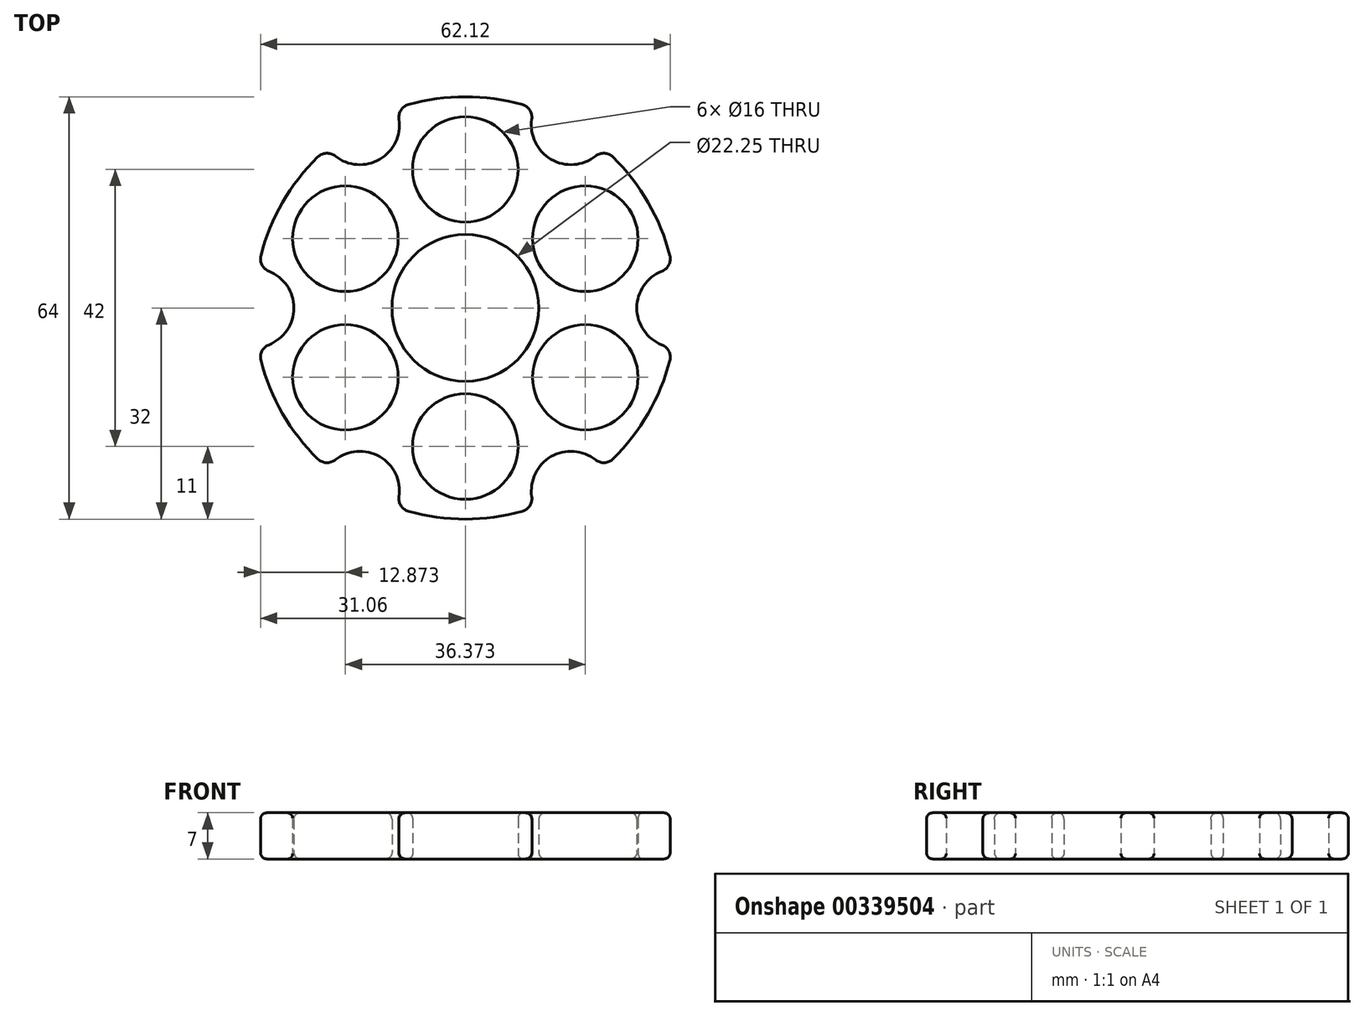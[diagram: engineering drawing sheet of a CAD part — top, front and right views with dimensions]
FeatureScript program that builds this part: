
annotation { "Feature Type Name" : "Feature", "Feature Type Description" : "" }
export const myFeature = defineFeature(function(context is Context, id is Id, definition is map)
    precondition{}
    {
        {
            var Q0;
            Q0=qCreatedBy(makeId("Top.planeOp"),FACE);
            var sketch = newSketch(context, id + "F0", { "sketchPlane" : qUnion([Q0])});
            skArc(sketch, "E0", {"start": v(-22.37, 22.88) * mm, "mid": v(-27.71, 16) * mm, "end": v(-31, 7.94) * mm});
            skCircle(sketch, "E1", {"center": v(0, 0) * mm, "radius": 11.12 * mm});
            skCircle(sketch, "E2", {"center": v(0, 21) * mm, "radius": 8 * mm});
            skCircle(sketch, "E3.1.0", {"center": v(-18.19, 10.5) * mm, "radius": 8 * mm});
            skCircle(sketch, "E3.2.0", {"center": v(-18.19, -10.5) * mm, "radius": 8 * mm});
            skCircle(sketch, "E3.3.0", {"center": v(0, -21) * mm, "radius": 8 * mm});
            skCircle(sketch, "E3.4.0", {"center": v(18.19, -10.5) * mm, "radius": 8 * mm});
            skCircle(sketch, "E3.5.0", {"center": v(18.19, 10.5) * mm, "radius": 8 * mm});
            skArc(sketch, "E4", {"start": v(-29.8, -5.58) * mm, "mid": v(-26, 0) * mm, "end": v(-29.8, 5.58) * mm});
            skArc(sketch, "E5.1.0", {"start": v(-10.07, -28.6) * mm, "mid": v(-13, -22.52) * mm, "end": v(-19.73, -23.01) * mm});
            skArc(sketch, "E5.2.0", {"start": v(19.73, -23.01) * mm, "mid": v(13, -22.52) * mm, "end": v(10.07, -28.6) * mm});
            skArc(sketch, "E5.3.0", {"start": v(29.8, 5.58) * mm, "mid": v(26, 0) * mm, "end": v(29.8, -5.58) * mm});
            skArc(sketch, "E5.4.0", {"start": v(10.07, 28.6) * mm, "mid": v(13, 22.52) * mm, "end": v(19.73, 23.01) * mm});
            skArc(sketch, "E5.5.0", {"start": v(-19.73, 23.01) * mm, "mid": v(-13, 22.52) * mm, "end": v(-10.07, 28.6) * mm});
            skArc(sketch, "E6.trimOffspring", {"start": v(8.63, 30.82) * mm, "mid": v(0, 32) * mm, "end": v(-8.63, 30.82) * mm});
            skArc(sketch, "E7.trimOffspring", {"start": v(31, 7.94) * mm, "mid": v(27.71, 16) * mm, "end": v(22.37, 22.88) * mm});
            skArc(sketch, "E8.trimOffspring", {"start": v(22.37, -22.88) * mm, "mid": v(27.71, -16) * mm, "end": v(31, -7.94) * mm});
            skArc(sketch, "E9.trimOffspring", {"start": v(-8.63, -30.82) * mm, "mid": v(0, -32) * mm, "end": v(8.63, -30.82) * mm});
            skArc(sketch, "E10.trimOffspring", {"start": v(-31, -7.94) * mm, "mid": v(-27.71, -16) * mm, "end": v(-22.37, -22.88) * mm});
            skPoint(sketch, "E11.visualSharp", {"position": v(-10.55, 30.21) * mm});
            skArc(sketch, "E11.filletArc", {"start": v(-8.63, 30.82) * mm, "mid": v(-9.77, 29.98) * mm, "end": v(-10.07, 28.6) * mm});
            skPoint(sketch, "E12.visualSharp", {"position": v(10.55, 30.21) * mm});
            skArc(sketch, "E12.filletArc", {"start": v(10.07, 28.6) * mm, "mid": v(9.77, 29.98) * mm, "end": v(8.63, 30.82) * mm});
            skPoint(sketch, "E13.visualSharp", {"position": v(20.9, 24.24) * mm});
            skArc(sketch, "E13.filletArc", {"start": v(22.37, 22.88) * mm, "mid": v(21.08, 23.45) * mm, "end": v(19.73, 23.01) * mm});
            skPoint(sketch, "E14.visualSharp", {"position": v(31.44, 5.97) * mm});
            skArc(sketch, "E14.filletArc", {"start": v(29.8, 5.58) * mm, "mid": v(30.84, 6.53) * mm, "end": v(31, 7.94) * mm});
            skPoint(sketch, "E15.visualSharp", {"position": v(31.44, -5.97) * mm});
            skArc(sketch, "E15.filletArc", {"start": v(31, -7.94) * mm, "mid": v(30.84, -6.53) * mm, "end": v(29.8, -5.58) * mm});
            skPoint(sketch, "E16.visualSharp", {"position": v(20.9, -24.24) * mm});
            skArc(sketch, "E16.filletArc", {"start": v(19.73, -23.01) * mm, "mid": v(21.08, -23.45) * mm, "end": v(22.37, -22.88) * mm});
            skPoint(sketch, "E17.visualSharp", {"position": v(10.55, -30.21) * mm});
            skArc(sketch, "E17.filletArc", {"start": v(8.63, -30.82) * mm, "mid": v(9.77, -29.98) * mm, "end": v(10.07, -28.6) * mm});
            skPoint(sketch, "E18.visualSharp", {"position": v(-10.55, -30.21) * mm});
            skArc(sketch, "E18.filletArc", {"start": v(-10.07, -28.6) * mm, "mid": v(-9.77, -29.98) * mm, "end": v(-8.63, -30.82) * mm});
            skPoint(sketch, "E19.visualSharp", {"position": v(-20.9, -24.24) * mm});
            skArc(sketch, "E19.filletArc", {"start": v(-22.37, -22.88) * mm, "mid": v(-21.08, -23.45) * mm, "end": v(-19.73, -23.01) * mm});
            skPoint(sketch, "E20.visualSharp", {"position": v(-31.44, -5.97) * mm});
            skArc(sketch, "E20.filletArc", {"start": v(-29.8, -5.58) * mm, "mid": v(-30.84, -6.53) * mm, "end": v(-31, -7.94) * mm});
            skPoint(sketch, "E21.visualSharp", {"position": v(-31.44, 5.97) * mm});
            skArc(sketch, "E21.filletArc", {"start": v(-31, 7.94) * mm, "mid": v(-30.84, 6.53) * mm, "end": v(-29.8, 5.58) * mm});
            skPoint(sketch, "E22.visualSharp", {"position": v(-20.9, 24.24) * mm});
            skArc(sketch, "E22.filletArc", {"start": v(-19.73, 23.01) * mm, "mid": v(-21.08, 23.45) * mm, "end": v(-22.37, 22.88) * mm});
            skSolve(sketch);
        }
        {
            var Q0;
            Q0 = qSketchRegion(id + "F0", true);
            extrude(context, id + "F1", {"entities" : qUnion([Q0]), "depth" : 7 * mm});
        }
        {
            var Q0;
            Q0=makeQuery(id+"F1.opExtrude","SWEPT_FACE",FACE,{"disambiguationData":[OSD([sQuery(id+"F0.wireOp",EDGE,"E1")])]});
            fillet(context, id + "F2", {"entities" : qUnion([Q0]), "radius" : 1 * mm, "tangentPropagation" : true, "allowEdgeOverflow" : false});
        }
        {
            var Q0;
            Q0=makeQuery(id+"F1.opExtrude","SWEPT_FACE",FACE,{"disambiguationData":[OSD([sQuery(id+"F0.wireOp",EDGE,"E2")])]});
            var Q1;
            Q1=makeQuery(id+"F1.opExtrude","SWEPT_FACE",FACE,{"disambiguationData":[OSD([sQuery(id+"F0.wireOp",EDGE,"E3.5.0")])]});
            var Q2;
            Q2=makeQuery(id+"F1.opExtrude","SWEPT_FACE",FACE,{"disambiguationData":[OSD([sQuery(id+"F0.wireOp",EDGE,"E3.4.0")])]});
            var Q3;
            Q3=makeQuery(id+"F1.opExtrude","SWEPT_FACE",FACE,{"disambiguationData":[OSD([sQuery(id+"F0.wireOp",EDGE,"E3.3.0")])]});
            var Q4;
            Q4=makeQuery(id+"F1.opExtrude","SWEPT_FACE",FACE,{"disambiguationData":[OSD([sQuery(id+"F0.wireOp",EDGE,"E3.2.0")])]});
            var Q5;
            Q5=makeQuery(id+"F1.opExtrude","SWEPT_FACE",FACE,{"disambiguationData":[OSD([sQuery(id+"F0.wireOp",EDGE,"E3.1.0")])]});
            fillet(context, id + "F3", {"entities" : qUnion([Q0, Q1, Q2, Q3, Q4, Q5]), "radius" : .8 * mm, "tangentPropagation" : true, "allowEdgeOverflow" : false});
        }
        {
            var Q0;
            Q0=makeQuery(id+"F1.opExtrude","CAP_FACE",FACE,{"disambiguationData":[OSD([sQuery(id+"F0.wireOp",EDGE,"E0"),sQuery(id+"F0.wireOp",EDGE,"E1"),sQuery(id+"F0.wireOp",EDGE,"E2"),sQuery(id+"F0.wireOp",EDGE,"E3.1.0"),sQuery(id+"F0.wireOp",EDGE,"E3.2.0"),sQuery(id+"F0.wireOp",EDGE,"E3.3.0"),sQuery(id+"F0.wireOp",EDGE,"E3.4.0"),sQuery(id+"F0.wireOp",EDGE,"E3.5.0"),sQuery(id+"F0.wireOp",EDGE,"E4"),sQuery(id+"F0.wireOp",EDGE,"E5.1.0"),sQuery(id+"F0.wireOp",EDGE,"E5.2.0"),sQuery(id+"F0.wireOp",EDGE,"E5.3.0"),sQuery(id+"F0.wireOp",EDGE,"E5.4.0"),sQuery(id+"F0.wireOp",EDGE,"E5.5.0"),sQuery(id+"F0.wireOp",EDGE,"E6.trimOffspring"),sQuery(id+"F0.wireOp",EDGE,"E7.trimOffspring"),sQuery(id+"F0.wireOp",EDGE,"E8.trimOffspring"),sQuery(id+"F0.wireOp",EDGE,"E9.trimOffspring"),sQuery(id+"F0.wireOp",EDGE,"E10.trimOffspring"),sQuery(id+"F0.wireOp",EDGE,"E11.filletArc"),sQuery(id+"F0.wireOp",EDGE,"E12.filletArc"),sQuery(id+"F0.wireOp",EDGE,"E13.filletArc"),sQuery(id+"F0.wireOp",EDGE,"E14.filletArc"),sQuery(id+"F0.wireOp",EDGE,"E15.filletArc"),sQuery(id+"F0.wireOp",EDGE,"E16.filletArc"),sQuery(id+"F0.wireOp",EDGE,"E17.filletArc"),sQuery(id+"F0.wireOp",EDGE,"E18.filletArc"),sQuery(id+"F0.wireOp",EDGE,"E19.filletArc"),sQuery(id+"F0.wireOp",EDGE,"E20.filletArc"),sQuery(id+"F0.wireOp",EDGE,"E21.filletArc"),sQuery(id+"F0.wireOp",EDGE,"E22.filletArc")])],"isStart":false});
            var Q1;
            Q1=makeQuery(id+"F1.opExtrude","CAP_FACE",FACE,{"disambiguationData":[OSD([sQuery(id+"F0.wireOp",EDGE,"E0"),sQuery(id+"F0.wireOp",EDGE,"E1"),sQuery(id+"F0.wireOp",EDGE,"E2"),sQuery(id+"F0.wireOp",EDGE,"E3.1.0"),sQuery(id+"F0.wireOp",EDGE,"E3.2.0"),sQuery(id+"F0.wireOp",EDGE,"E3.3.0"),sQuery(id+"F0.wireOp",EDGE,"E3.4.0"),sQuery(id+"F0.wireOp",EDGE,"E3.5.0"),sQuery(id+"F0.wireOp",EDGE,"E4"),sQuery(id+"F0.wireOp",EDGE,"E5.1.0"),sQuery(id+"F0.wireOp",EDGE,"E5.2.0"),sQuery(id+"F0.wireOp",EDGE,"E5.3.0"),sQuery(id+"F0.wireOp",EDGE,"E5.4.0"),sQuery(id+"F0.wireOp",EDGE,"E5.5.0"),sQuery(id+"F0.wireOp",EDGE,"E6.trimOffspring"),sQuery(id+"F0.wireOp",EDGE,"E7.trimOffspring"),sQuery(id+"F0.wireOp",EDGE,"E8.trimOffspring"),sQuery(id+"F0.wireOp",EDGE,"E9.trimOffspring"),sQuery(id+"F0.wireOp",EDGE,"E10.trimOffspring"),sQuery(id+"F0.wireOp",EDGE,"E11.filletArc"),sQuery(id+"F0.wireOp",EDGE,"E12.filletArc"),sQuery(id+"F0.wireOp",EDGE,"E13.filletArc"),sQuery(id+"F0.wireOp",EDGE,"E14.filletArc"),sQuery(id+"F0.wireOp",EDGE,"E15.filletArc"),sQuery(id+"F0.wireOp",EDGE,"E16.filletArc"),sQuery(id+"F0.wireOp",EDGE,"E17.filletArc"),sQuery(id+"F0.wireOp",EDGE,"E18.filletArc"),sQuery(id+"F0.wireOp",EDGE,"E19.filletArc"),sQuery(id+"F0.wireOp",EDGE,"E20.filletArc"),sQuery(id+"F0.wireOp",EDGE,"E21.filletArc"),sQuery(id+"F0.wireOp",EDGE,"E22.filletArc")])],"isStart":true});
            fillet(context, id + "F4", {"entities" : qUnion([Q0, Q1]), "radius" : 1 * mm, "tangentPropagation" : true, "allowEdgeOverflow" : false});
        }
    });
